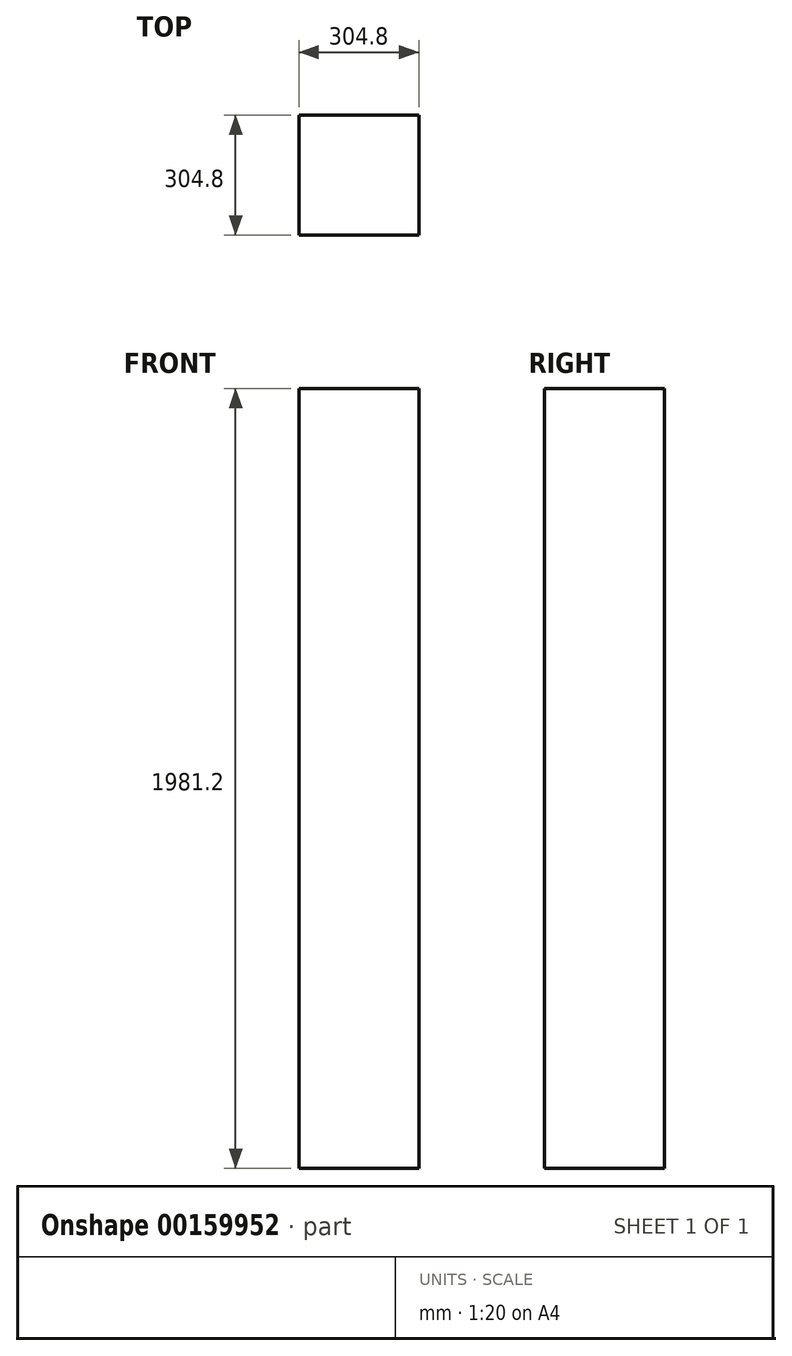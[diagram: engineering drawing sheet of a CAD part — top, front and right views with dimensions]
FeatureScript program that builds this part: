
annotation { "Feature Type Name" : "Feature", "Feature Type Description" : "" }
export const myFeature = defineFeature(function(context is Context, id is Id, definition is map)
    precondition{}
    {
        {
            var Q0;
            Q0=qCreatedBy(makeId("Top.planeOp"),FACE);
            var sketch = newSketch(context, id + "F0", { "sketchPlane" : qUnion([Q0])});
            skLineSegment(sketch, "E0.bottom", {"start": v(-30.81, 276.57) * mm, "end": v(273.99, 276.57) * mm});
            skLineSegment(sketch, "E0.top", {"start": v(-30.81, -28.23) * mm, "end": v(273.99, -28.23) * mm});
            skLineSegment(sketch, "E0.left", {"start": v(-30.81, 276.57) * mm, "end": v(-30.81, -28.23) * mm});
            skLineSegment(sketch, "E0.right", {"start": v(273.99, 276.57) * mm, "end": v(273.99, -28.23) * mm});
            skSolve(sketch);
        }
        {
            var Q0;
            Q0=makeQuery(id+"F0.imprint","IMPRINT",FACE,{"disambiguationData":[TD([[makeQuery(id+"F0.imprint","IMPRINT",EDGE,{"derivedFrom":sQuery(id+"F0.wireOp",EDGE,"E0.bottom")}),-1.0]])]});
            extrude(context, id + "F1", {"entities" : qUnion([Q0]), "depth" : 1981.2 * mm});
        }
    });
